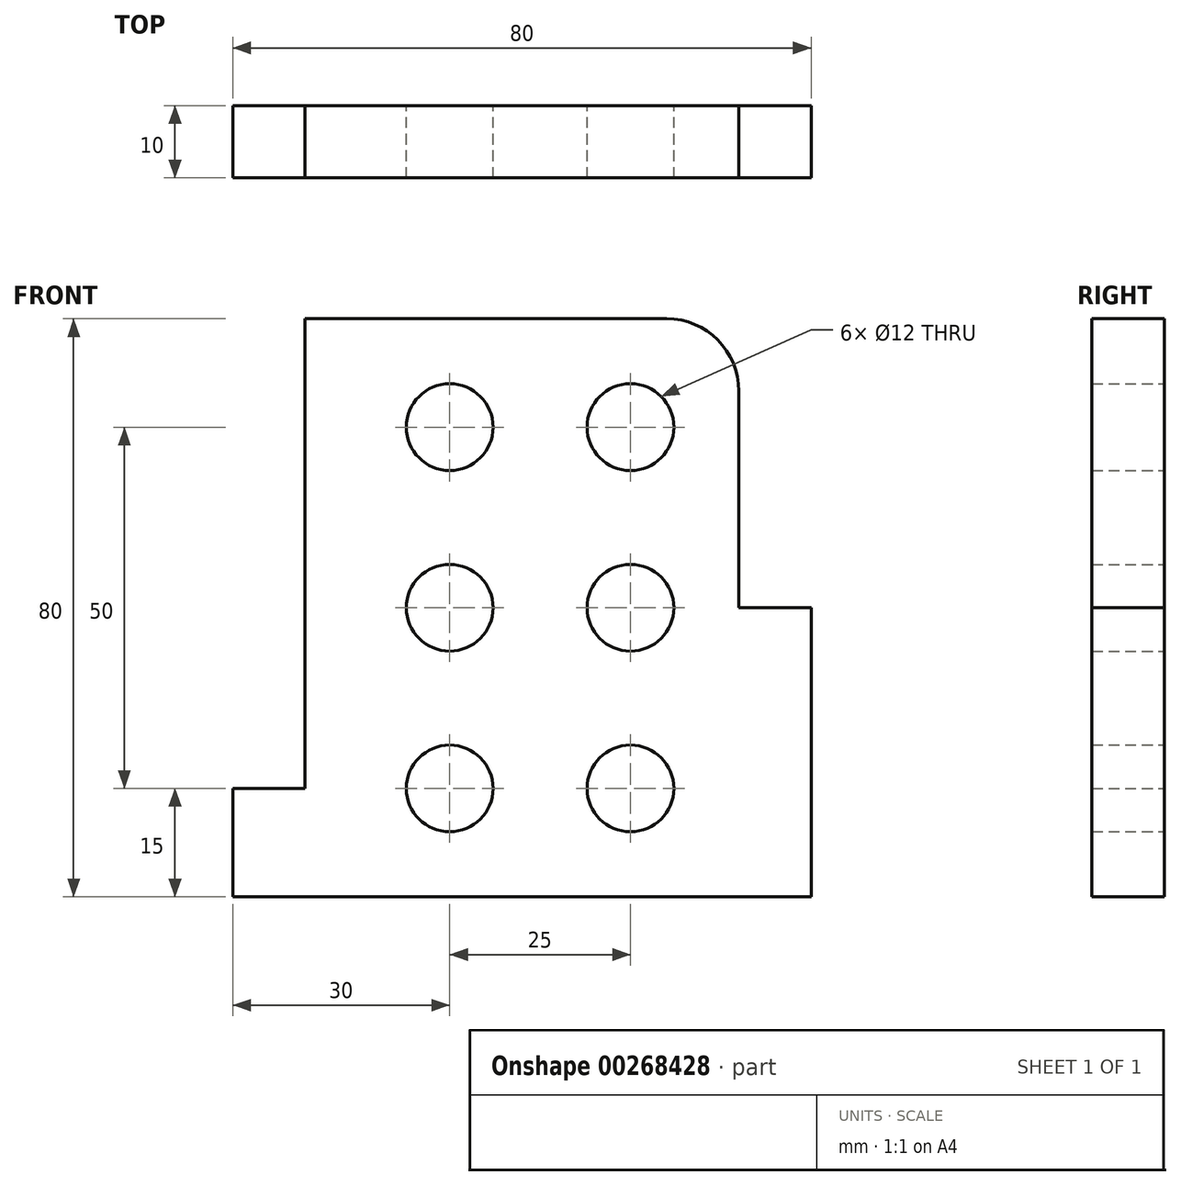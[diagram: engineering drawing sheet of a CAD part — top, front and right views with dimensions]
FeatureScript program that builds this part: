
annotation { "Feature Type Name" : "Feature", "Feature Type Description" : "" }
export const myFeature = defineFeature(function(context is Context, id is Id, definition is map)
    precondition{}
    {
        {
            var Q0;
            Q0=qCreatedBy(makeId("Front.planeOp"),FACE);
            var sketch = newSketch(context, id + "F0", { "sketchPlane" : qUnion([Q0])});
            skLineSegment(sketch, "E0", {"start": v(0, 0) * mm, "end": v(80, 0) * mm});
            skLineSegment(sketch, "E1", {"start": v(80, 0) * mm, "end": v(80, 40) * mm});
            skLineSegment(sketch, "E2", {"start": v(80, 40) * mm, "end": v(70, 40) * mm});
            skLineSegment(sketch, "E3", {"start": v(70, 40) * mm, "end": v(70, 70) * mm});
            skLineSegment(sketch, "E4", {"start": v(10, 80) * mm, "end": v(10, 15) * mm});
            skLineSegment(sketch, "E5", {"start": v(10, 15) * mm, "end": v(0, 15) * mm});
            skLineSegment(sketch, "E6", {"start": v(0, 15) * mm, "end": v(0, 0) * mm});
            skLineSegment(sketch, "E7.bottom", {"start": v(30, 65) * mm, "end": v(55, 65) * mm, "construction": true});
            skLineSegment(sketch, "E7.top", {"start": v(30, 15) * mm, "end": v(55, 15) * mm, "construction": true});
            skLineSegment(sketch, "E7.left", {"start": v(30, 65) * mm, "end": v(30, 15) * mm, "construction": true});
            skLineSegment(sketch, "E7.right", {"start": v(55, 65) * mm, "end": v(55, 15) * mm, "construction": true});
            skLineSegment(sketch, "E8", {"start": v(30, 40) * mm, "end": v(55, 40) * mm, "construction": true});
            skCircle(sketch, "E9", {"center": v(30, 65) * mm, "radius": 6 * mm});
            skCircle(sketch, "E10", {"center": v(55, 65) * mm, "radius": 6 * mm});
            skCircle(sketch, "E11", {"center": v(55, 40) * mm, "radius": 6 * mm});
            skCircle(sketch, "E12", {"center": v(30, 40) * mm, "radius": 6 * mm});
            skCircle(sketch, "E13", {"center": v(30, 15) * mm, "radius": 6 * mm});
            skCircle(sketch, "E14", {"center": v(55, 15) * mm, "radius": 6 * mm});
            skLineSegment(sketch, "E15", {"start": v(10, 80) * mm, "end": v(60, 80) * mm});
            skArc(sketch, "E16", {"start": v(70, 70) * mm, "mid": v(67.07, 77.07) * mm, "end": v(60, 80) * mm});
            skSolve(sketch);
        }
        {
            var Q0;
            Q0 = qSketchRegion(id + "F0", true);
            extrude(context, id + "F1", {"entities" : qUnion([Q0]), "depth" : 10 * mm});
        }
    });
